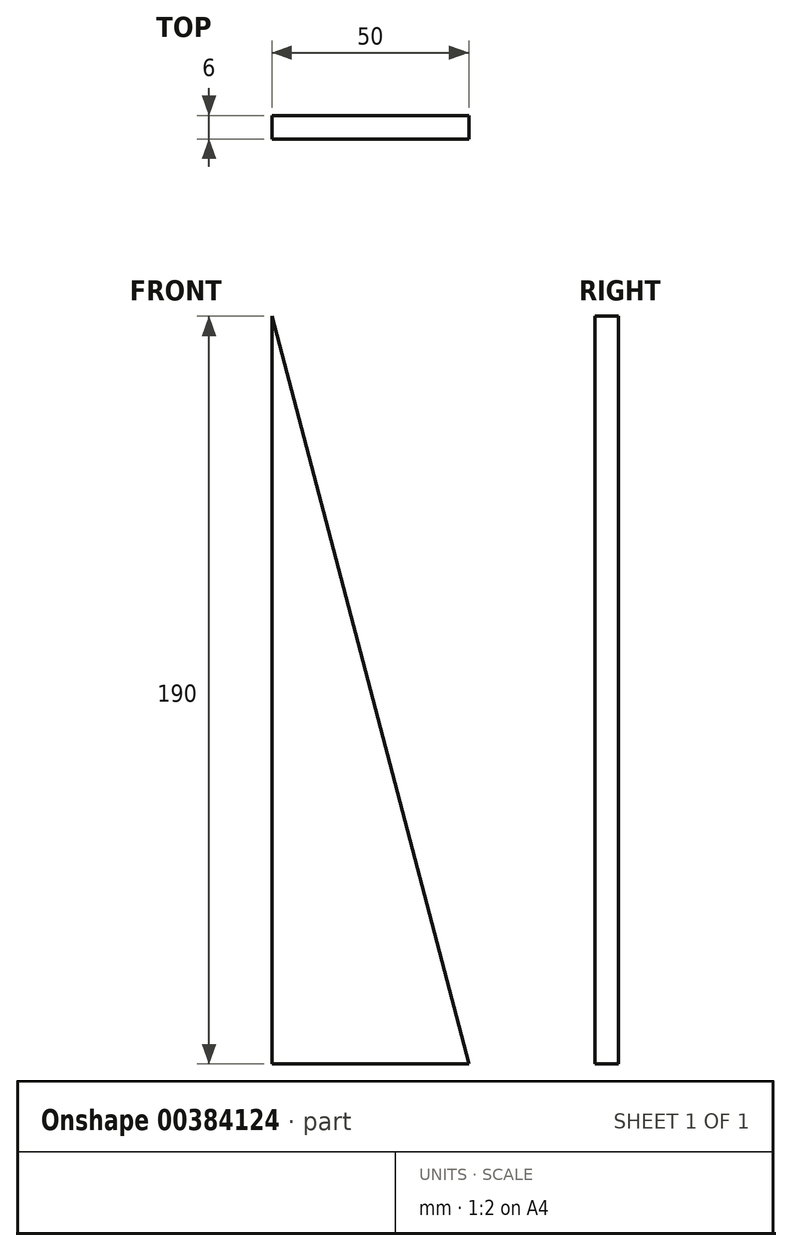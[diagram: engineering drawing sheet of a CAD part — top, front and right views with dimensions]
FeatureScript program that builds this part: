
annotation { "Feature Type Name" : "Feature", "Feature Type Description" : "" }
export const myFeature = defineFeature(function(context is Context, id is Id, definition is map)
    precondition{}
    {
        {
            var Q0;
            Q0=qCreatedBy(makeId("Front.planeOp"),FACE);
            var sketch = newSketch(context, id + "F0", { "sketchPlane" : qUnion([Q0])});
            skLineSegment(sketch, "E0.bottom", {"start": v(0, 0) * mm, "end": v(50, 0) * mm});
            skLineSegment(sketch, "E0.left", {"start": v(0, 0) * mm, "end": v(0, 190) * mm});
            skLineSegment(sketch, "E1", {"start": v(0, 190) * mm, "end": v(50, 0) * mm});
            skSolve(sketch);
        }
        {
            var Q0;
            Q0=makeQuery(id+"F0.imprint","IMPRINT",FACE,{"disambiguationData":[TD([[makeQuery(id+"F0.imprint","IMPRINT",EDGE,{"derivedFrom":sQuery(id+"F0.wireOp",EDGE,"E0.bottom")}),1.0]])]});
            extrude(context, id + "F1", {"entities" : qUnion([Q0]), "depth" : 6 * mm});
        }
    });
